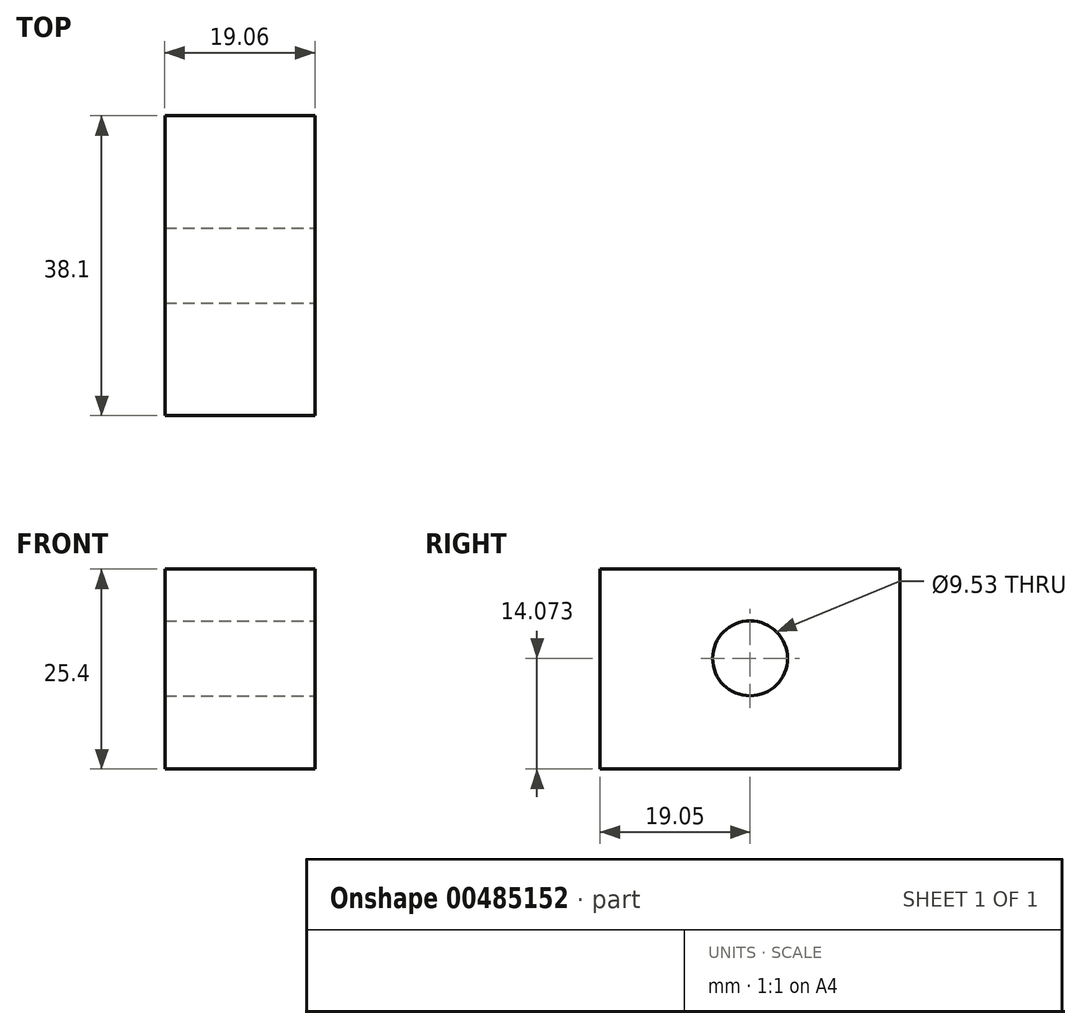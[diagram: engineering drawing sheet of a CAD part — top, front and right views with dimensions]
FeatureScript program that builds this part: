
annotation { "Feature Type Name" : "Feature", "Feature Type Description" : "" }
export const myFeature = defineFeature(function(context is Context, id is Id, definition is map)
    precondition{}
    {
        {
            var Q0;
            Q0=qCreatedBy(makeId("Top.planeOp"),FACE);
            var sketch = newSketch(context, id + "F0", { "sketchPlane" : qUnion([Q0])});
            skLineSegment(sketch, "E0.bottom", {"start": v(9.53, 19.05) * mm, "end": v(-9.52, 19.05) * mm});
            skLineSegment(sketch, "E0.top", {"start": v(9.52, -19.05) * mm, "end": v(-9.53, -19.05) * mm});
            skLineSegment(sketch, "E0.left", {"start": v(9.53, 19.05) * mm, "end": v(9.52, -19.05) * mm});
            skLineSegment(sketch, "E0.right", {"start": v(-9.52, 19.05) * mm, "end": v(-9.53, -19.05) * mm});
            skPoint(sketch, "E0.middle", {"position": v(0, 0) * mm});
            skSolve(sketch);
        }
        {
            var Q0;
            Q0 = qSketchRegion(id + "F0", true);
            extrude(context, id + "F1", {"entities" : qUnion([Q0]), "depth" : 25.4 * mm});
        }
        {
            var Q0;
            Q0=makeQuery(id+"F1.opExtrude","SWEPT_FACE",FACE,{"disambiguationData":[OSD([sQuery(id+"F0.wireOp",EDGE,"E0.left")])]});
            var sketch = newSketch(context, id + "F2", { "sketchPlane" : qUnion([Q0])});
            skCircle(sketch, "E1", {"center": v(0, 14.07) * mm, "radius": 4.76 * mm});
            skSolve(sketch);
        }
        {
            var Q0;
            Q0=sQuery(id+"F2.wireOp",VERTEX,"E1.center");
            var Q1;
            Q1=makeQuery(id+"F1.opExtrude","SWEPT_BODY",BODY,{"disambiguationData":[OSD([sQuery(id+"F0.wireOp",EDGE,"E0.bottom"),sQuery(id+"F0.wireOp",EDGE,"E0.top"),sQuery(id+"F0.wireOp",EDGE,"E0.left"),sQuery(id+"F0.wireOp",EDGE,"E0.right")])]});
            hole(context, id + "F3", {"style" : HoleStyle.SIMPLE, "endStyle" : HoleEndStyle.THROUGH, "holeDiameter" : 9.52 * mm, "isTappedThrough" : true, "tappedDepth" : 12.7 * mm, "tapClearance" : 3, "locations" : qUnion([Q0]), "scope" : qUnion([Q1])});
        }
    });
